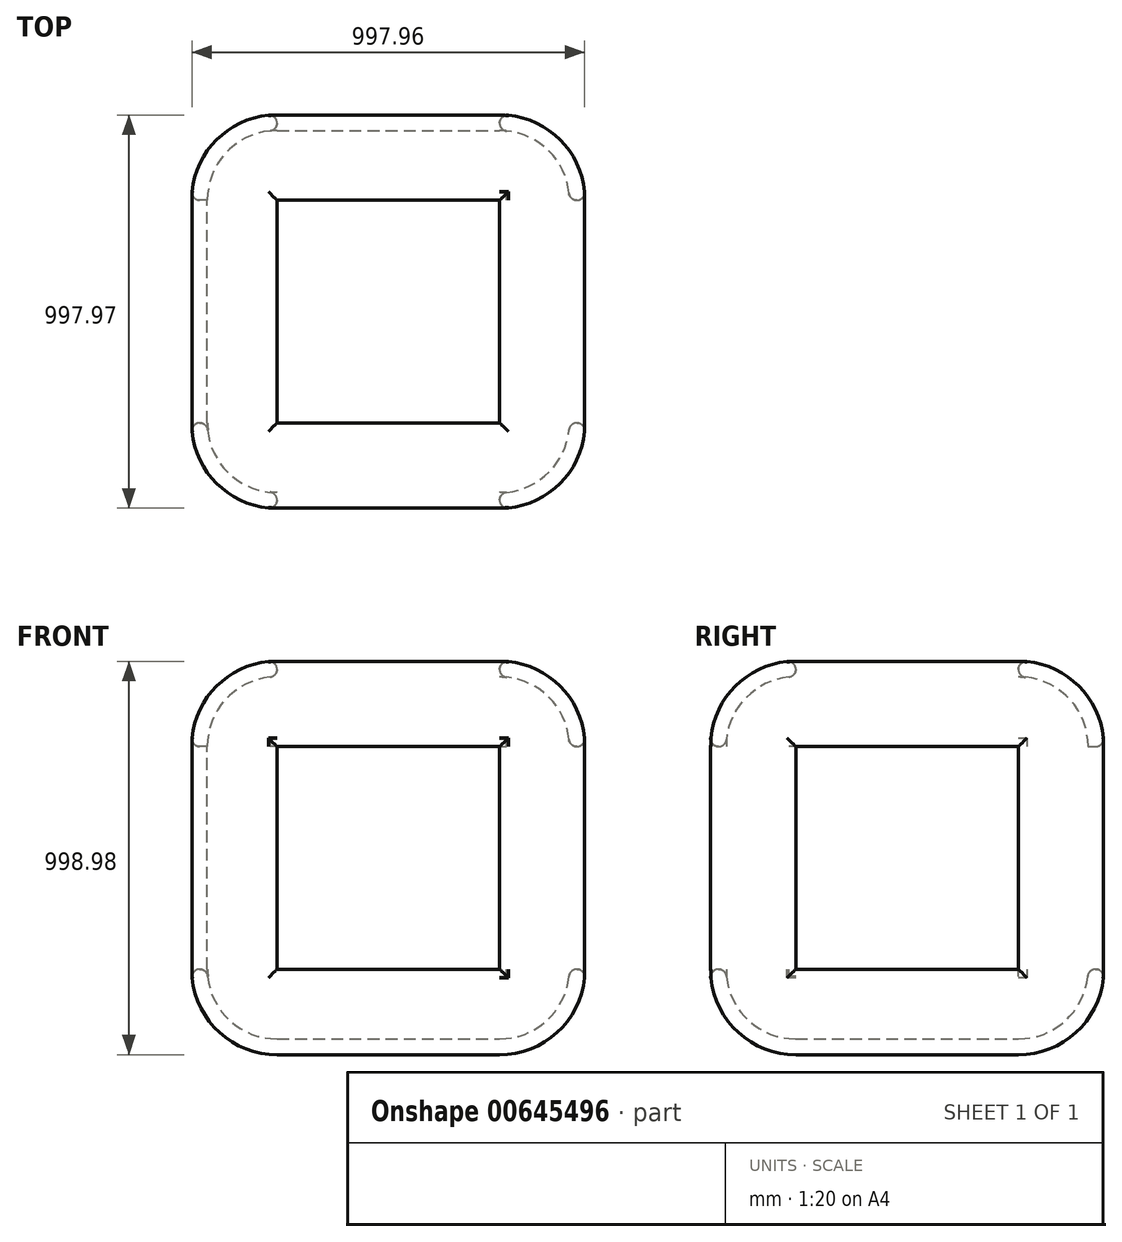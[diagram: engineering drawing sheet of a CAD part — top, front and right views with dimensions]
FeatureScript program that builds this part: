
annotation { "Feature Type Name" : "Feature", "Feature Type Description" : "" }
export const myFeature = defineFeature(function(context is Context, id is Id, definition is map)
    precondition{}
    {
        {
            var Q0;
            Q0=qCreatedBy(makeId("Top.planeOp"),FACE);
            var sketch = newSketch(context, id + "F0", { "sketchPlane" : qUnion([Q0])});
            skLineSegment(sketch, "E0.bottom", {"start": v(-747.7, 327.33) * mm, "end": v(252.3, 327.33) * mm});
            skLineSegment(sketch, "E0.top", {"start": v(-747.7, -672.67) * mm, "end": v(252.3, -672.67) * mm});
            skLineSegment(sketch, "E0.left", {"start": v(-747.7, 327.33) * mm, "end": v(-747.7, -672.67) * mm});
            skLineSegment(sketch, "E0.right", {"start": v(252.3, 327.33) * mm, "end": v(252.3, -672.67) * mm});
            skSolve(sketch);
        }
        {
            var Q0;
            Q0=makeQuery(id+"F0.imprint","IMPRINT",FACE,{"disambiguationData":[TD([[makeQuery(id+"F0.imprint","IMPRINT",EDGE,{"derivedFrom":sQuery(id+"F0.wireOp",EDGE,"E0.bottom")}),-1.0]])]});
            extrude(context, id + "F1", {"entities" : qUnion([Q0]), "depth" : 1000 * mm, "offsetDistance" : 25 * mm});
        }
        {
            var Q0;
            Q0=makeQuery(id+"F1.opExtrude","CAP_EDGE",EDGE,{"disambiguationData":[OSD([sQuery(id+"F0.wireOp",EDGE,"E0.bottom")])],"isStart":false});
            var Q1;
            Q1=makeQuery(id+"F1.opExtrude","CAP_EDGE",EDGE,{"disambiguationData":[OSD([sQuery(id+"F0.wireOp",EDGE,"E0.left")])],"isStart":false});
            var Q2;
            Q2=makeQuery(id+"F1.opExtrude","SWEPT_EDGE",EDGE,{"disambiguationData":[OSD([sQuery(id+"F0.wireOp",EDGE,"E0.bottom"),sQuery(id+"F0.wireOp",EDGE,"E0.left")])]});
            var Q3;
            Q3=makeQuery(id+"F1.opExtrude","CAP_EDGE",EDGE,{"disambiguationData":[OSD([sQuery(id+"F0.wireOp",EDGE,"E0.left")])],"isStart":true});
            var Q4;
            Q4=makeQuery(id+"F1.opExtrude","CAP_EDGE",EDGE,{"disambiguationData":[OSD([sQuery(id+"F0.wireOp",EDGE,"E0.bottom")])],"isStart":true});
            var Q5;
            Q5=makeQuery(id+"F1.opExtrude","SWEPT_EDGE",EDGE,{"disambiguationData":[OSD([sQuery(id+"F0.wireOp",EDGE,"E0.top"),sQuery(id+"F0.wireOp",EDGE,"E0.left")])]});
            var Q6;
            Q6=makeQuery(id+"F1.opExtrude","CAP_EDGE",EDGE,{"disambiguationData":[OSD([sQuery(id+"F0.wireOp",EDGE,"E0.top")])],"isStart":false});
            var Q7;
            Q7=makeQuery(id+"F1.opExtrude","CAP_EDGE",EDGE,{"disambiguationData":[OSD([sQuery(id+"F0.wireOp",EDGE,"E0.top")])],"isStart":true});
            var Q8;
            Q8=makeQuery(id+"F1.opExtrude","SWEPT_EDGE",EDGE,{"disambiguationData":[OSD([sQuery(id+"F0.wireOp",EDGE,"E0.top"),sQuery(id+"F0.wireOp",EDGE,"E0.right")])]});
            var Q9;
            Q9=makeQuery(id+"F1.opExtrude","CAP_EDGE",EDGE,{"disambiguationData":[OSD([sQuery(id+"F0.wireOp",EDGE,"E0.right")])],"isStart":false});
            var Q10;
            Q10=makeQuery(id+"F1.opExtrude","CAP_EDGE",EDGE,{"disambiguationData":[OSD([sQuery(id+"F0.wireOp",EDGE,"E0.right")])],"isStart":true});
            var Q11;
            Q11=makeQuery(id+"F1.opExtrude","SWEPT_EDGE",EDGE,{"disambiguationData":[OSD([sQuery(id+"F0.wireOp",EDGE,"E0.bottom"),sQuery(id+"F0.wireOp",EDGE,"E0.right")])]});
            fillet(context, id + "F2", {"entities" : qUnion([Q0, Q1, Q2, Q3, Q4, Q5, Q6, Q7, Q8, Q9, Q10, Q11]), "radius" : 217.28 * mm, "tangentPropagation" : true, "allowEdgeOverflow" : false});
        }
        {
            var Q0;
            Q0=makeQuery(id+"F1.opExtrude","SWEPT_FACE",FACE,{"disambiguationData":[OSD([sQuery(id+"F0.wireOp",EDGE,"E0.left")])]});
            var Q1;
            Q1=makeQuery(id+"F1.opExtrude","SWEPT_FACE",FACE,{"disambiguationData":[OSD([sQuery(id+"F0.wireOp",EDGE,"E0.bottom")])]});
            var Q2;
            Q2=makeQuery(id+"F1.opExtrude","SWEPT_FACE",FACE,{"disambiguationData":[OSD([sQuery(id+"F0.wireOp",EDGE,"E0.right")])]});
            var Q3;
            Q3=makeQuery(id+"F1.opExtrude","CAP_FACE",FACE,{"disambiguationData":[OSD([sQuery(id+"F0.wireOp",EDGE,"E0.bottom"),sQuery(id+"F0.wireOp",EDGE,"E0.top"),sQuery(id+"F0.wireOp",EDGE,"E0.left"),sQuery(id+"F0.wireOp",EDGE,"E0.right")])],"isStart":false});
            var Q4;
            Q4=makeQuery(id+"F1.opExtrude","SWEPT_FACE",FACE,{"disambiguationData":[OSD([sQuery(id+"F0.wireOp",EDGE,"E0.top")])]});
            shell(context, id + "F3", {"entities" : qUnion([Q0, Q1, Q2, Q3, Q4]), "thickness" : 40 * mm});
        }
        {
            var Q0;
            {var subQ0=sQuery(id+"F0.wireOp",EDGE,"E0.right");Q0=makeQuery(id+"F2.opFillet","BLEND_EDGE",EDGE,{"blendedFrom":[makeQuery(id+"F1.opExtrude","CAP_EDGE",EDGE,{"disambiguationData":[OSD([subQ0])],"isStart":false}),makeQuery(id+"F1.opExtrude","CAP_FACE",FACE,{"disambiguationData":[OSD([sQuery(id+"F0.wireOp",EDGE,"E0.bottom"),sQuery(id+"F0.wireOp",EDGE,"E0.top"),sQuery(id+"F0.wireOp",EDGE,"E0.left"),subQ0])],"isStart":false})],"blendedInto":[makeQuery(id+"F1.opExtrude","CAP_FACE",FACE,{"disambiguationData":[OSD([sQuery(id+"F0.wireOp",EDGE,"E0.bottom"),sQuery(id+"F0.wireOp",EDGE,"E0.top"),sQuery(id+"F0.wireOp",EDGE,"E0.left"),subQ0])],"isStart":false})]});}
            var Q1;
            {var subQ0=sQuery(id+"F0.wireOp",EDGE,"E0.right");var subQ1=sQuery(id+"F0.wireOp",EDGE,"E0.left");var subQ2=sQuery(id+"F0.wireOp",EDGE,"E0.top");var subQ3=sQuery(id+"F0.wireOp",EDGE,"E0.bottom");Q1=makeQuery(id+"F3.opShell","OFFSET_EDGE",EDGE,{"disambiguationData":[OSD([subQ3,subQ2,subQ1,subQ0]),TDD([makeQuery(id+"F2.opFillet","BLEND_EDGE",EDGE,{"blendedFrom":[makeQuery(id+"F1.opExtrude","CAP_EDGE",EDGE,{"disambiguationData":[OSD([subQ0])],"isStart":false}),makeQuery(id+"F1.opExtrude","CAP_FACE",FACE,{"disambiguationData":[OSD([subQ3,subQ2,subQ1,subQ0])],"isStart":false})],"blendedInto":[makeQuery(id+"F1.opExtrude","CAP_FACE",FACE,{"disambiguationData":[OSD([subQ3,subQ2,subQ1,subQ0])],"isStart":false})]})])]});}
            var Q2;
            {var subQ0=sQuery(id+"F0.wireOp",EDGE,"E0.top");Q2=makeQuery(id+"F2.opFillet","BLEND_EDGE",EDGE,{"blendedFrom":[makeQuery(id+"F1.opExtrude","CAP_EDGE",EDGE,{"disambiguationData":[OSD([subQ0])],"isStart":false}),makeQuery(id+"F1.opExtrude","CAP_FACE",FACE,{"disambiguationData":[OSD([sQuery(id+"F0.wireOp",EDGE,"E0.bottom"),subQ0,sQuery(id+"F0.wireOp",EDGE,"E0.left"),sQuery(id+"F0.wireOp",EDGE,"E0.right")])],"isStart":false})],"blendedInto":[makeQuery(id+"F1.opExtrude","CAP_FACE",FACE,{"disambiguationData":[OSD([sQuery(id+"F0.wireOp",EDGE,"E0.bottom"),subQ0,sQuery(id+"F0.wireOp",EDGE,"E0.left"),sQuery(id+"F0.wireOp",EDGE,"E0.right")])],"isStart":false})]});}
            var Q3;
            {var subQ0=sQuery(id+"F0.wireOp",EDGE,"E0.right");var subQ1=sQuery(id+"F0.wireOp",EDGE,"E0.left");var subQ2=sQuery(id+"F0.wireOp",EDGE,"E0.top");var subQ3=sQuery(id+"F0.wireOp",EDGE,"E0.bottom");Q3=makeQuery(id+"F3.opShell","OFFSET_EDGE",EDGE,{"disambiguationData":[OSD([subQ3,subQ2,subQ1,subQ0]),TDD([makeQuery(id+"F2.opFillet","BLEND_EDGE",EDGE,{"blendedFrom":[makeQuery(id+"F1.opExtrude","CAP_EDGE",EDGE,{"disambiguationData":[OSD([subQ2])],"isStart":false}),makeQuery(id+"F1.opExtrude","CAP_FACE",FACE,{"disambiguationData":[OSD([subQ3,subQ2,subQ1,subQ0])],"isStart":false})],"blendedInto":[makeQuery(id+"F1.opExtrude","CAP_FACE",FACE,{"disambiguationData":[OSD([subQ3,subQ2,subQ1,subQ0])],"isStart":false})]})])]});}
            var Q4;
            {var subQ0=sQuery(id+"F0.wireOp",EDGE,"E0.bottom");Q4=makeQuery(id+"F2.opFillet","BLEND_EDGE",EDGE,{"blendedFrom":[makeQuery(id+"F1.opExtrude","CAP_EDGE",EDGE,{"disambiguationData":[OSD([subQ0])],"isStart":false}),makeQuery(id+"F1.opExtrude","CAP_FACE",FACE,{"disambiguationData":[OSD([subQ0,sQuery(id+"F0.wireOp",EDGE,"E0.top"),sQuery(id+"F0.wireOp",EDGE,"E0.left"),sQuery(id+"F0.wireOp",EDGE,"E0.right")])],"isStart":false})],"blendedInto":[makeQuery(id+"F1.opExtrude","CAP_FACE",FACE,{"disambiguationData":[OSD([subQ0,sQuery(id+"F0.wireOp",EDGE,"E0.top"),sQuery(id+"F0.wireOp",EDGE,"E0.left"),sQuery(id+"F0.wireOp",EDGE,"E0.right")])],"isStart":false})]});}
            var Q5;
            {var subQ0=sQuery(id+"F0.wireOp",EDGE,"E0.right");var subQ1=sQuery(id+"F0.wireOp",EDGE,"E0.left");var subQ2=sQuery(id+"F0.wireOp",EDGE,"E0.top");var subQ3=sQuery(id+"F0.wireOp",EDGE,"E0.bottom");Q5=makeQuery(id+"F3.opShell","OFFSET_EDGE",EDGE,{"disambiguationData":[OSD([subQ3,subQ2,subQ1,subQ0]),TDD([makeQuery(id+"F2.opFillet","BLEND_EDGE",EDGE,{"blendedFrom":[makeQuery(id+"F1.opExtrude","CAP_EDGE",EDGE,{"disambiguationData":[OSD([subQ3])],"isStart":false}),makeQuery(id+"F1.opExtrude","CAP_FACE",FACE,{"disambiguationData":[OSD([subQ3,subQ2,subQ1,subQ0])],"isStart":false})],"blendedInto":[makeQuery(id+"F1.opExtrude","CAP_FACE",FACE,{"disambiguationData":[OSD([subQ3,subQ2,subQ1,subQ0])],"isStart":false})]})])]});}
            var Q6;
            {var subQ0=sQuery(id+"F0.wireOp",EDGE,"E0.left");Q6=makeQuery(id+"F2.opFillet","BLEND_EDGE",EDGE,{"blendedFrom":[makeQuery(id+"F1.opExtrude","CAP_EDGE",EDGE,{"disambiguationData":[OSD([subQ0])],"isStart":false}),makeQuery(id+"F1.opExtrude","CAP_FACE",FACE,{"disambiguationData":[OSD([sQuery(id+"F0.wireOp",EDGE,"E0.bottom"),sQuery(id+"F0.wireOp",EDGE,"E0.top"),subQ0,sQuery(id+"F0.wireOp",EDGE,"E0.right")])],"isStart":false})],"blendedInto":[makeQuery(id+"F1.opExtrude","CAP_FACE",FACE,{"disambiguationData":[OSD([sQuery(id+"F0.wireOp",EDGE,"E0.bottom"),sQuery(id+"F0.wireOp",EDGE,"E0.top"),subQ0,sQuery(id+"F0.wireOp",EDGE,"E0.right")])],"isStart":false})]});}
            var Q7;
            {var subQ0=sQuery(id+"F0.wireOp",EDGE,"E0.right");var subQ1=sQuery(id+"F0.wireOp",EDGE,"E0.left");var subQ2=sQuery(id+"F0.wireOp",EDGE,"E0.top");var subQ3=sQuery(id+"F0.wireOp",EDGE,"E0.bottom");Q7=makeQuery(id+"F3.opShell","OFFSET_EDGE",EDGE,{"disambiguationData":[OSD([subQ3,subQ2,subQ1,subQ0]),TDD([makeQuery(id+"F2.opFillet","BLEND_EDGE",EDGE,{"blendedFrom":[makeQuery(id+"F1.opExtrude","CAP_EDGE",EDGE,{"disambiguationData":[OSD([subQ1])],"isStart":false}),makeQuery(id+"F1.opExtrude","CAP_FACE",FACE,{"disambiguationData":[OSD([subQ3,subQ2,subQ1,subQ0])],"isStart":false})],"blendedInto":[makeQuery(id+"F1.opExtrude","CAP_FACE",FACE,{"disambiguationData":[OSD([subQ3,subQ2,subQ1,subQ0])],"isStart":false})]})])]});}
            var Q8;
            {var subQ0=sQuery(id+"F0.wireOp",EDGE,"E0.top");Q8=makeQuery(id+"F2.opFillet","BLEND_EDGE",EDGE,{"blendedFrom":[makeQuery(id+"F1.opExtrude","SWEPT_EDGE",EDGE,{"disambiguationData":[OSD([subQ0,sQuery(id+"F0.wireOp",EDGE,"E0.left")])]}),makeQuery(id+"F1.opExtrude","SWEPT_FACE",FACE,{"disambiguationData":[OSD([subQ0])]})],"blendedInto":[makeQuery(id+"F1.opExtrude","SWEPT_FACE",FACE,{"disambiguationData":[OSD([subQ0])]})]});}
            var Q9;
            {var subQ0=sQuery(id+"F0.wireOp",EDGE,"E0.top");var subQ1=sQuery(id+"F0.wireOp",EDGE,"E0.left");Q9=makeQuery(id+"F3.opShell","OFFSET_EDGE",EDGE,{"disambiguationData":[OSD([subQ0,subQ1]),TDD([makeQuery(id+"F2.opFillet","BLEND_EDGE",EDGE,{"blendedFrom":[makeQuery(id+"F1.opExtrude","SWEPT_EDGE",EDGE,{"disambiguationData":[OSD([subQ0,subQ1])]}),makeQuery(id+"F1.opExtrude","SWEPT_FACE",FACE,{"disambiguationData":[OSD([subQ0])]})],"blendedInto":[makeQuery(id+"F1.opExtrude","SWEPT_FACE",FACE,{"disambiguationData":[OSD([subQ0])]})]})])]});}
            var Q10;
            {var subQ0=sQuery(id+"F0.wireOp",EDGE,"E0.top");Q10=makeQuery(id+"F2.opFillet","BLEND_EDGE",EDGE,{"blendedFrom":[makeQuery(id+"F1.opExtrude","CAP_EDGE",EDGE,{"disambiguationData":[OSD([subQ0])],"isStart":true}),makeQuery(id+"F1.opExtrude","SWEPT_FACE",FACE,{"disambiguationData":[OSD([subQ0])]})],"blendedInto":[makeQuery(id+"F1.opExtrude","SWEPT_FACE",FACE,{"disambiguationData":[OSD([subQ0])]})]});}
            var Q11;
            {var subQ0=sQuery(id+"F0.wireOp",EDGE,"E0.top");Q11=makeQuery(id+"F3.opShell","OFFSET_EDGE",EDGE,{"disambiguationData":[OSD([subQ0]),TDD([makeQuery(id+"F2.opFillet","BLEND_EDGE",EDGE,{"blendedFrom":[makeQuery(id+"F1.opExtrude","CAP_EDGE",EDGE,{"disambiguationData":[OSD([subQ0])],"isStart":true}),makeQuery(id+"F1.opExtrude","SWEPT_FACE",FACE,{"disambiguationData":[OSD([subQ0])]})],"blendedInto":[makeQuery(id+"F1.opExtrude","SWEPT_FACE",FACE,{"disambiguationData":[OSD([subQ0])]})]})])]});}
            var Q12;
            {var subQ0=sQuery(id+"F0.wireOp",EDGE,"E0.left");Q12=makeQuery(id+"F3.opShell","OFFSET_EDGE",EDGE,{"disambiguationData":[OSD([subQ0]),TDD([makeQuery(id+"F2.opFillet","BLEND_EDGE",EDGE,{"blendedFrom":[makeQuery(id+"F1.opExtrude","CAP_EDGE",EDGE,{"disambiguationData":[OSD([subQ0])],"isStart":true}),makeQuery(id+"F1.opExtrude","SWEPT_FACE",FACE,{"disambiguationData":[OSD([subQ0])]})],"blendedInto":[makeQuery(id+"F1.opExtrude","SWEPT_FACE",FACE,{"disambiguationData":[OSD([subQ0])]})]})])]});}
            var Q13;
            {var subQ0=sQuery(id+"F0.wireOp",EDGE,"E0.left");Q13=makeQuery(id+"F2.opFillet","BLEND_EDGE",EDGE,{"blendedFrom":[makeQuery(id+"F1.opExtrude","CAP_EDGE",EDGE,{"disambiguationData":[OSD([subQ0])],"isStart":true}),makeQuery(id+"F1.opExtrude","SWEPT_FACE",FACE,{"disambiguationData":[OSD([subQ0])]})],"blendedInto":[makeQuery(id+"F1.opExtrude","SWEPT_FACE",FACE,{"disambiguationData":[OSD([subQ0])]})]});}
            var Q14;
            {var subQ0=sQuery(id+"F0.wireOp",EDGE,"E0.right");Q14=makeQuery(id+"F2.opFillet","BLEND_EDGE",EDGE,{"blendedFrom":[makeQuery(id+"F1.opExtrude","CAP_EDGE",EDGE,{"disambiguationData":[OSD([subQ0])],"isStart":true}),makeQuery(id+"F1.opExtrude","SWEPT_FACE",FACE,{"disambiguationData":[OSD([subQ0])]})],"blendedInto":[makeQuery(id+"F1.opExtrude","SWEPT_FACE",FACE,{"disambiguationData":[OSD([subQ0])]})]});}
            var Q15;
            {var subQ0=sQuery(id+"F0.wireOp",EDGE,"E0.right");Q15=makeQuery(id+"F3.opShell","OFFSET_EDGE",EDGE,{"disambiguationData":[OSD([subQ0]),TDD([makeQuery(id+"F2.opFillet","BLEND_EDGE",EDGE,{"blendedFrom":[makeQuery(id+"F1.opExtrude","CAP_EDGE",EDGE,{"disambiguationData":[OSD([subQ0])],"isStart":true}),makeQuery(id+"F1.opExtrude","SWEPT_FACE",FACE,{"disambiguationData":[OSD([subQ0])]})],"blendedInto":[makeQuery(id+"F1.opExtrude","SWEPT_FACE",FACE,{"disambiguationData":[OSD([subQ0])]})]})])]});}
            var Q16;
            {var subQ0=sQuery(id+"F0.wireOp",EDGE,"E0.bottom");Q16=makeQuery(id+"F2.opFillet","BLEND_EDGE",EDGE,{"blendedFrom":[makeQuery(id+"F1.opExtrude","CAP_EDGE",EDGE,{"disambiguationData":[OSD([subQ0])],"isStart":true}),makeQuery(id+"F1.opExtrude","SWEPT_FACE",FACE,{"disambiguationData":[OSD([subQ0])]})],"blendedInto":[makeQuery(id+"F1.opExtrude","SWEPT_FACE",FACE,{"disambiguationData":[OSD([subQ0])]})]});}
            var Q17;
            {var subQ0=sQuery(id+"F0.wireOp",EDGE,"E0.bottom");Q17=makeQuery(id+"F3.opShell","OFFSET_EDGE",EDGE,{"disambiguationData":[OSD([subQ0]),TDD([makeQuery(id+"F2.opFillet","BLEND_EDGE",EDGE,{"blendedFrom":[makeQuery(id+"F1.opExtrude","CAP_EDGE",EDGE,{"disambiguationData":[OSD([subQ0])],"isStart":true}),makeQuery(id+"F1.opExtrude","SWEPT_FACE",FACE,{"disambiguationData":[OSD([subQ0])]})],"blendedInto":[makeQuery(id+"F1.opExtrude","SWEPT_FACE",FACE,{"disambiguationData":[OSD([subQ0])]})]})])]});}
            var Q18;
            {var subQ0=sQuery(id+"F0.wireOp",EDGE,"E0.right");Q18=makeQuery(id+"F2.opFillet","BLEND_EDGE",EDGE,{"blendedFrom":[makeQuery(id+"F1.opExtrude","SWEPT_EDGE",EDGE,{"disambiguationData":[OSD([sQuery(id+"F0.wireOp",EDGE,"E0.top"),subQ0])]}),makeQuery(id+"F1.opExtrude","SWEPT_FACE",FACE,{"disambiguationData":[OSD([subQ0])]})],"blendedInto":[makeQuery(id+"F1.opExtrude","SWEPT_FACE",FACE,{"disambiguationData":[OSD([subQ0])]})]});}
            var Q19;
            {var subQ0=sQuery(id+"F0.wireOp",EDGE,"E0.right");var subQ1=sQuery(id+"F0.wireOp",EDGE,"E0.top");Q19=makeQuery(id+"F3.opShell","OFFSET_EDGE",EDGE,{"disambiguationData":[OSD([subQ1,subQ0]),TDD([makeQuery(id+"F2.opFillet","BLEND_EDGE",EDGE,{"blendedFrom":[makeQuery(id+"F1.opExtrude","SWEPT_EDGE",EDGE,{"disambiguationData":[OSD([subQ1,subQ0])]}),makeQuery(id+"F1.opExtrude","SWEPT_FACE",FACE,{"disambiguationData":[OSD([subQ0])]})],"blendedInto":[makeQuery(id+"F1.opExtrude","SWEPT_FACE",FACE,{"disambiguationData":[OSD([subQ0])]})]})])]});}
            var Q20;
            {var subQ0=sQuery(id+"F0.wireOp",EDGE,"E0.right");var subQ1=sQuery(id+"F0.wireOp",EDGE,"E0.bottom");Q20=makeQuery(id+"F3.opShell","OFFSET_EDGE",EDGE,{"disambiguationData":[OSD([subQ1,subQ0]),TDD([makeQuery(id+"F2.opFillet","BLEND_EDGE",EDGE,{"blendedFrom":[makeQuery(id+"F1.opExtrude","SWEPT_EDGE",EDGE,{"disambiguationData":[OSD([subQ1,subQ0])]}),makeQuery(id+"F1.opExtrude","SWEPT_FACE",FACE,{"disambiguationData":[OSD([subQ0])]})],"blendedInto":[makeQuery(id+"F1.opExtrude","SWEPT_FACE",FACE,{"disambiguationData":[OSD([subQ0])]})]})])]});}
            var Q21;
            {var subQ0=sQuery(id+"F0.wireOp",EDGE,"E0.right");Q21=makeQuery(id+"F2.opFillet","BLEND_EDGE",EDGE,{"blendedFrom":[makeQuery(id+"F1.opExtrude","SWEPT_EDGE",EDGE,{"disambiguationData":[OSD([sQuery(id+"F0.wireOp",EDGE,"E0.bottom"),subQ0])]}),makeQuery(id+"F1.opExtrude","SWEPT_FACE",FACE,{"disambiguationData":[OSD([subQ0])]})],"blendedInto":[makeQuery(id+"F1.opExtrude","SWEPT_FACE",FACE,{"disambiguationData":[OSD([subQ0])]})]});}
            var Q22;
            {var subQ0=sQuery(id+"F0.wireOp",EDGE,"E0.bottom");var subQ1=sQuery(id+"F0.wireOp",EDGE,"E0.left");Q22=makeQuery(id+"F3.opShell","OFFSET_EDGE",EDGE,{"disambiguationData":[OSD([subQ0,subQ1]),TDD([makeQuery(id+"F2.opFillet","BLEND_EDGE",EDGE,{"blendedFrom":[makeQuery(id+"F1.opExtrude","SWEPT_EDGE",EDGE,{"disambiguationData":[OSD([subQ0,subQ1])]}),makeQuery(id+"F1.opExtrude","SWEPT_FACE",FACE,{"disambiguationData":[OSD([subQ0])]})],"blendedInto":[makeQuery(id+"F1.opExtrude","SWEPT_FACE",FACE,{"disambiguationData":[OSD([subQ0])]})]})])]});}
            var Q23;
            {var subQ0=sQuery(id+"F0.wireOp",EDGE,"E0.bottom");Q23=makeQuery(id+"F2.opFillet","BLEND_EDGE",EDGE,{"blendedFrom":[makeQuery(id+"F1.opExtrude","SWEPT_EDGE",EDGE,{"disambiguationData":[OSD([subQ0,sQuery(id+"F0.wireOp",EDGE,"E0.left")])]}),makeQuery(id+"F1.opExtrude","SWEPT_FACE",FACE,{"disambiguationData":[OSD([subQ0])]})],"blendedInto":[makeQuery(id+"F1.opExtrude","SWEPT_FACE",FACE,{"disambiguationData":[OSD([subQ0])]})]});}
            var Q24;
            {var subQ0=sQuery(id+"F0.wireOp",EDGE,"E0.top");Q24=makeQuery(id+"F2.opFillet","BLEND_EDGE",EDGE,{"blendedFrom":[makeQuery(id+"F1.opExtrude","CAP_EDGE",EDGE,{"disambiguationData":[OSD([subQ0])],"isStart":false}),makeQuery(id+"F1.opExtrude","SWEPT_FACE",FACE,{"disambiguationData":[OSD([subQ0])]})],"blendedInto":[makeQuery(id+"F1.opExtrude","SWEPT_FACE",FACE,{"disambiguationData":[OSD([subQ0])]})]});}
            var Q25;
            {var subQ0=sQuery(id+"F0.wireOp",EDGE,"E0.top");Q25=makeQuery(id+"F3.opShell","OFFSET_EDGE",EDGE,{"disambiguationData":[OSD([subQ0]),TDD([makeQuery(id+"F2.opFillet","BLEND_EDGE",EDGE,{"blendedFrom":[makeQuery(id+"F1.opExtrude","CAP_EDGE",EDGE,{"disambiguationData":[OSD([subQ0])],"isStart":false}),makeQuery(id+"F1.opExtrude","SWEPT_FACE",FACE,{"disambiguationData":[OSD([subQ0])]})],"blendedInto":[makeQuery(id+"F1.opExtrude","SWEPT_FACE",FACE,{"disambiguationData":[OSD([subQ0])]})]})])]});}
            var Q26;
            {var subQ0=sQuery(id+"F0.wireOp",EDGE,"E0.right");Q26=makeQuery(id+"F2.opFillet","BLEND_EDGE",EDGE,{"blendedFrom":[makeQuery(id+"F1.opExtrude","CAP_EDGE",EDGE,{"disambiguationData":[OSD([subQ0])],"isStart":false}),makeQuery(id+"F1.opExtrude","SWEPT_FACE",FACE,{"disambiguationData":[OSD([subQ0])]})],"blendedInto":[makeQuery(id+"F1.opExtrude","SWEPT_FACE",FACE,{"disambiguationData":[OSD([subQ0])]})]});}
            var Q27;
            {var subQ0=sQuery(id+"F0.wireOp",EDGE,"E0.right");Q27=makeQuery(id+"F3.opShell","OFFSET_EDGE",EDGE,{"disambiguationData":[OSD([subQ0]),TDD([makeQuery(id+"F2.opFillet","BLEND_EDGE",EDGE,{"blendedFrom":[makeQuery(id+"F1.opExtrude","CAP_EDGE",EDGE,{"disambiguationData":[OSD([subQ0])],"isStart":false}),makeQuery(id+"F1.opExtrude","SWEPT_FACE",FACE,{"disambiguationData":[OSD([subQ0])]})],"blendedInto":[makeQuery(id+"F1.opExtrude","SWEPT_FACE",FACE,{"disambiguationData":[OSD([subQ0])]})]})])]});}
            var Q28;
            {var subQ0=sQuery(id+"F0.wireOp",EDGE,"E0.top");Q28=makeQuery(id+"F2.opFillet","BLEND_EDGE",EDGE,{"blendedFrom":[makeQuery(id+"F1.opExtrude","SWEPT_EDGE",EDGE,{"disambiguationData":[OSD([subQ0,sQuery(id+"F0.wireOp",EDGE,"E0.right")])]}),makeQuery(id+"F1.opExtrude","SWEPT_FACE",FACE,{"disambiguationData":[OSD([subQ0])]})],"blendedInto":[makeQuery(id+"F1.opExtrude","SWEPT_FACE",FACE,{"disambiguationData":[OSD([subQ0])]})]});}
            var Q29;
            {var subQ0=sQuery(id+"F0.wireOp",EDGE,"E0.top");var subQ1=sQuery(id+"F0.wireOp",EDGE,"E0.right");Q29=makeQuery(id+"F3.opShell","OFFSET_EDGE",EDGE,{"disambiguationData":[OSD([subQ0,subQ1]),TDD([makeQuery(id+"F2.opFillet","BLEND_EDGE",EDGE,{"blendedFrom":[makeQuery(id+"F1.opExtrude","SWEPT_EDGE",EDGE,{"disambiguationData":[OSD([subQ0,subQ1])]}),makeQuery(id+"F1.opExtrude","SWEPT_FACE",FACE,{"disambiguationData":[OSD([subQ0])]})],"blendedInto":[makeQuery(id+"F1.opExtrude","SWEPT_FACE",FACE,{"disambiguationData":[OSD([subQ0])]})]})])]});}
            var Q30;
            {var subQ0=sQuery(id+"F0.wireOp",EDGE,"E0.left");var subQ1=sQuery(id+"F0.wireOp",EDGE,"E0.top");Q30=makeQuery(id+"F3.opShell","OFFSET_EDGE",EDGE,{"disambiguationData":[OSD([subQ1,subQ0]),TDD([makeQuery(id+"F2.opFillet","BLEND_EDGE",EDGE,{"blendedFrom":[makeQuery(id+"F1.opExtrude","SWEPT_EDGE",EDGE,{"disambiguationData":[OSD([subQ1,subQ0])]}),makeQuery(id+"F1.opExtrude","SWEPT_FACE",FACE,{"disambiguationData":[OSD([subQ0])]})],"blendedInto":[makeQuery(id+"F1.opExtrude","SWEPT_FACE",FACE,{"disambiguationData":[OSD([subQ0])]})]})])]});}
            var Q31;
            {var subQ0=sQuery(id+"F0.wireOp",EDGE,"E0.left");Q31=makeQuery(id+"F2.opFillet","BLEND_EDGE",EDGE,{"blendedFrom":[makeQuery(id+"F1.opExtrude","SWEPT_EDGE",EDGE,{"disambiguationData":[OSD([sQuery(id+"F0.wireOp",EDGE,"E0.top"),subQ0])]}),makeQuery(id+"F1.opExtrude","SWEPT_FACE",FACE,{"disambiguationData":[OSD([subQ0])]})],"blendedInto":[makeQuery(id+"F1.opExtrude","SWEPT_FACE",FACE,{"disambiguationData":[OSD([subQ0])]})]});}
            var Q32;
            {var subQ0=sQuery(id+"F0.wireOp",EDGE,"E0.bottom");var subQ1=sQuery(id+"F0.wireOp",EDGE,"E0.right");Q32=makeQuery(id+"F3.opShell","OFFSET_EDGE",EDGE,{"disambiguationData":[OSD([subQ0,subQ1]),TDD([makeQuery(id+"F2.opFillet","BLEND_EDGE",EDGE,{"blendedFrom":[makeQuery(id+"F1.opExtrude","SWEPT_EDGE",EDGE,{"disambiguationData":[OSD([subQ0,subQ1])]}),makeQuery(id+"F1.opExtrude","SWEPT_FACE",FACE,{"disambiguationData":[OSD([subQ0])]})],"blendedInto":[makeQuery(id+"F1.opExtrude","SWEPT_FACE",FACE,{"disambiguationData":[OSD([subQ0])]})]})])]});}
            var Q33;
            {var subQ0=sQuery(id+"F0.wireOp",EDGE,"E0.bottom");Q33=makeQuery(id+"F2.opFillet","BLEND_EDGE",EDGE,{"blendedFrom":[makeQuery(id+"F1.opExtrude","SWEPT_EDGE",EDGE,{"disambiguationData":[OSD([subQ0,sQuery(id+"F0.wireOp",EDGE,"E0.right")])]}),makeQuery(id+"F1.opExtrude","SWEPT_FACE",FACE,{"disambiguationData":[OSD([subQ0])]})],"blendedInto":[makeQuery(id+"F1.opExtrude","SWEPT_FACE",FACE,{"disambiguationData":[OSD([subQ0])]})]});}
            fillet(context, id + "F4", {"entities" : qUnion([Q0, Q1, Q2, Q3, Q4, Q5, Q6, Q7, Q8, Q9, Q10, Q11, Q12, Q13, Q14, Q15, Q16, Q17, Q18, Q19, Q20, Q21, Q22, Q23, Q24, Q25, Q26, Q27, Q28, Q29, Q30, Q31, Q32, Q33]), "radius" : 20 * mm, "tangentPropagation" : true, "allowEdgeOverflow" : false});
        }
    });
